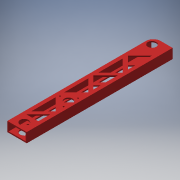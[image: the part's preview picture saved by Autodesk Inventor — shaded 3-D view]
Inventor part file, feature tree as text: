
AUTODESK INVENTOR PART (.ipt)
format: ipt  version: 2017 SP1 (Build 210196100, 196)  size: 248,832 bytes
history: native  units: in
note: dims shown in document units (in); Inventor stores cm internally (conversion verified against a paired STEP export)
features: extrude x4, sketch x4, fillet x2, projected_geometry x1
ambient origin geometry x8: Origin, YZ Plane, XZ Plane, XY Plane, X Axis, Y Axis, Z Axis, Center Point
bodies: Solid1 (feature_tree)
feature tree (11):
  extrude  "Extrusion1"  Depth=2.0in
  extrude  "Extrusion2"  Depth=0.125in TaperAngle=0.0deg
  fillet  "Fillet1"  Radius=0.877in
  extrude  "Extrusion3"  Depth=0.875in TaperAngle=0.0deg
  extrude  "Extrusion4"  Depth=0.75in
  fillet  "Fillet2"  Radius=0.625in
  sketch  "Sketch1"  dims[d0=1.0in d1=2.0in]
  sketch  "Sketch2"  dims[d2=0.125in d3=19.25in d4=0.0in d5=0.877in]
  sketch  "Sketch3"  dims[d10=0.875in d11=20.0in d12=0.0in]
  projected_geometry  "Projected Loop1"
  sketch  "Sketch4"  dims[d13=0.75in d16=0.75in d17=0.625in d20=0.75in d21=0.625in d23=0.625in d24=1.5in d27=1.125in d28=0.15in d29=0.875in d30=0.375in d31=4.201in d32=0.375in d33=1.75in d34=1.0in d35=0.0in d36=0.875in d37=0.75in d38=1.0in d39=0.0in d40=0.75in]
